# Revit family: ON5MHX-NRG
name_source: partatom
category: Mechanical Equipment
units: mm (PartAtom-declared; Revit-internal decimal feet)

## family parameters
Always vertical = Yes
Cut with Voids When Loaded = No
OmniClass Number = 23.40.40.11.17
OmniClass Title = Refrigerated Cases
Part Type = Normal
Room Calculation Point = No
Round Connector Dimension = Use Radius
Shared = No
Work Plane-Based = Yes

## types (4) — shared parameters
18" Shelf = Yes
BOTTOM ELECTRICAL = Yes
BOTTOM REFRIGERATION PIPING = Yes
BTUH Conventional = 1646
BTUH Parallel = 1440
Certifications = NSF 7, UL471, CSA
DATE = 05/25/2016
DESIGNERS NAME = SHIDDRAMESH
DRAIN PIPING = Yes
Default Elevation = 48"
Defrosts Per Day = 6
Description = High arrow Multi-Deck Merchandiser
Discharge Air (°F) = 30 °F
Discharge Air Velocity (FPM) = 240 FPM
EQUIPMENT DESCRIPTION = High arrow Multi-Deck Merchandiser
EQUIPMENT MARK = ON5MHX-NRG
Evaporator (°F) = 26 °F
GLASS = Glass
Height = 85 5/8"
High Power (Cornice) Amps = 0 A
Item Description = High arrow Multi-Deck Merchandiser
LF STD END = Yes
Legend Number = ON5MHX-NRG
Manufacturer = HILL PHOENIX
Model = ON5MHX-NRG
PAINTED METAL UPPER SHELF = PAINTED SHELVES
REAR REFRIGERATION PIPING = Yes
REFRIGERATION PIPING = COPPER PIPE
RT STD END = Yes
STAINLESS STEEL = GALVANIZED STEEL
Standard Power Amps = 0 A
Superheat Set Point @ Bulb (°F) = 6-8 °F
TOP ELECTRICAL = Yes
TOP REFRIGERATION PIPING = Yes
Timed-Off Defrost Fail-Safe (Min) = 40 (Min)
Timed-Off Defrost Termination Temp = 42 °F
URL = http://www.hillphoenix.com
Width = 35 7/8"

## per-type parameters (varying)
| type | CENTER LINE | DRAIN LINE | High Efficiency Amps | High Efficiency Watts | High Power (Cornice) Watts | Length | Length of Cases | Light Length | Lights Per Row | Number of Fans | Refgn | Standard Power Watts |
| 12' | 72" | 72" | 1 A | 106 W | 45 W | 144" | 144" | 4' | 3 | 6 | 8 3/4" | 18 W |
| 8' | 48" | 48" | 1 A | 70 W | 30 W | 96" | 48" | 4' | 2 | 4 | 8 3/4" | 12 W |
| 6' | 36" | 36" | 1 A | 70 W | 24 W | 72" | 48" | 3' | 2 | 4 | 8 3/4" | 9 W |
| 4' | 24" | 36" | 0 A | 36 W | 15 W | 48" | 48" | 4' | 1 | 2 | 7 5/8" | 6 W |

## geometry (parser evidence)
native form markers: Blend x17, Sweep x7
no freeform markers — native parametric forms only
